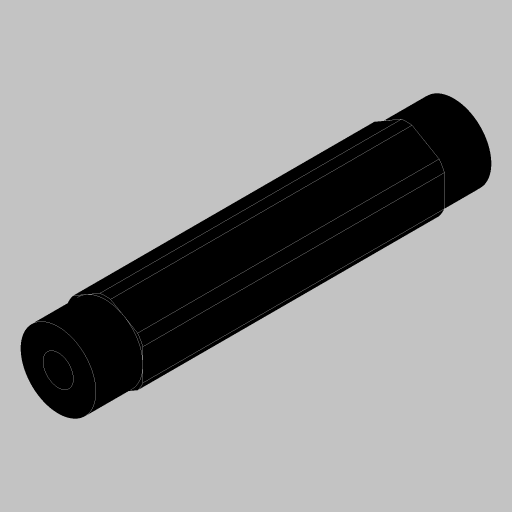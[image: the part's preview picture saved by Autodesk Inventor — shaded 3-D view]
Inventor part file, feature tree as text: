
AUTODESK INVENTOR PART (.ipt)
format: ipt  version: 2023.5 (Build 275446000, 446)  size: 168,448 bytes
history: native  units: in
note: dims shown in document units (in); Inventor stores cm internally (conversion verified against a paired STEP export)
features: extrude x3, projected_geometry x3, hole x1, mirror x1, sketch x1
ambient origin geometry x8: Origin, YZ Plane, XZ Plane, XY Plane, X Axis, Y Axis, Z Axis, Center Point
bodies: Solid1 (feature_tree)
feature tree (9):
  extrude  "Extrusion1"  Depth=0.5in
  hole  "Hole1"  [1 undecoded]
  extrude  "Extrusion3"  Depth=0.312in TaperAngle=0.0deg
  extrude  "Extrusion4"  Depth=0.5in
  mirror  "Mirror2"
  sketch  "Sketch5"  dims[d2=0.0in d9=0.625in d10=0.385in d11=0.25in d12=0.5635in d13=1.0in d14=0.8108in d16=0.7in d17=0.0in d18=0.0in d19=0.312in d20=0.0in d21=0.5in]
  projected_geometry  "Projected Loop2"
  projected_geometry  "Project Cut Edges1"
  projected_geometry  "Project Cut Edges2"
note: 1 required parameter value undecoded (feature->parameter linkage not recoverable at this tier; creation-order binding heuristic only, values carry confidence <= 0.55)
